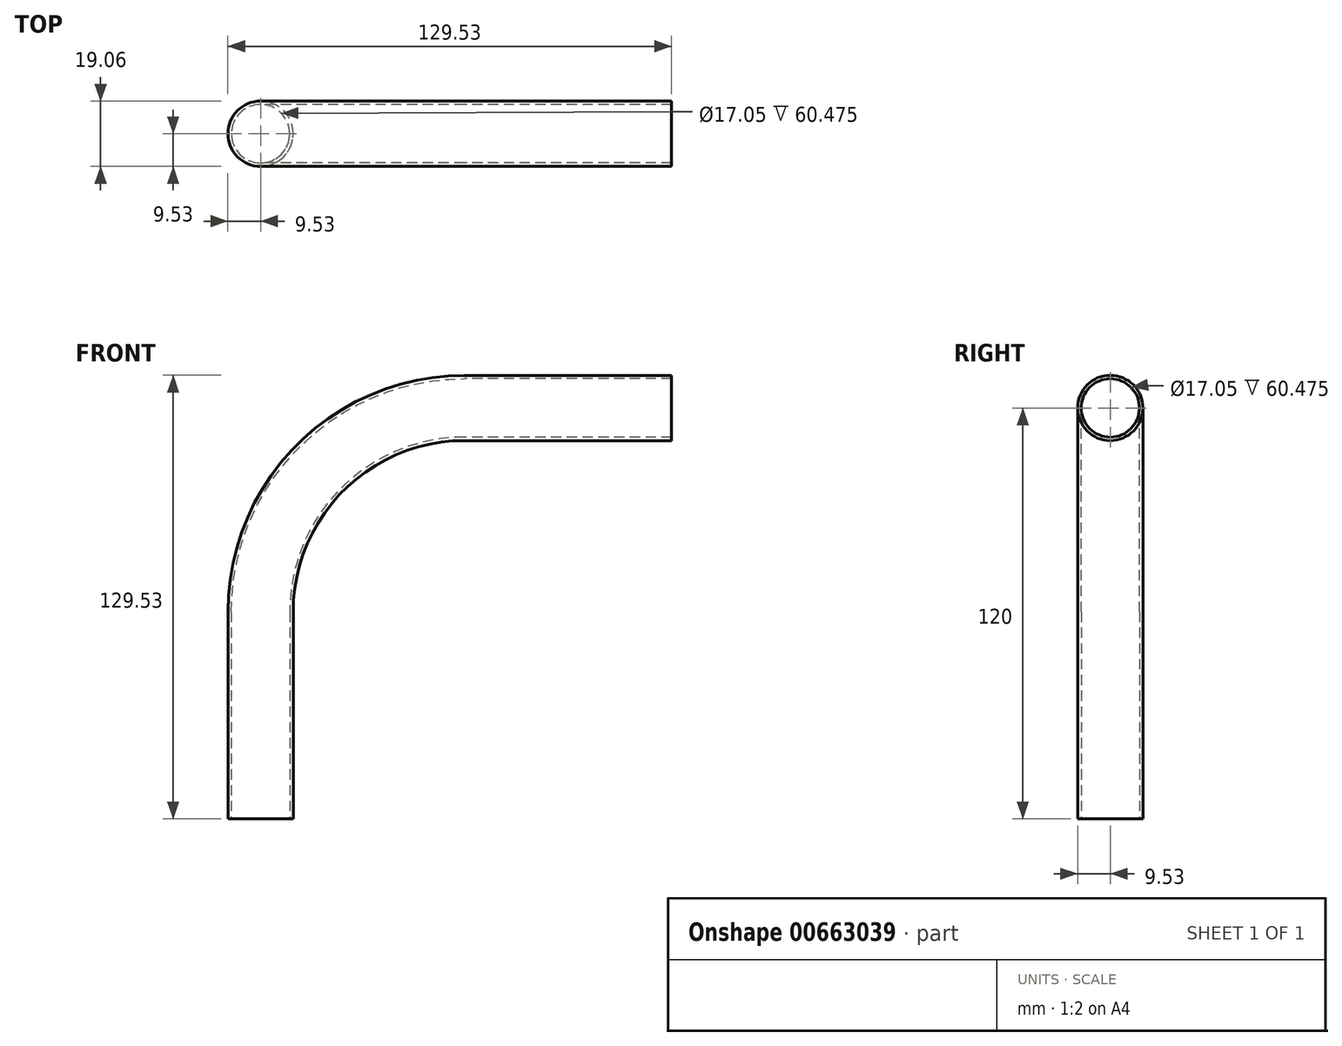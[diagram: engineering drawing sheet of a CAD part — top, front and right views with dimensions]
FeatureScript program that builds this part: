
annotation { "Feature Type Name" : "Feature", "Feature Type Description" : "" }
export const myFeature = defineFeature(function(context is Context, id is Id, definition is map)
    precondition{}
    {
        {
            var Q0;
            Q0=qCreatedBy(makeId("Front.planeOp"),FACE);
            var sketch = newSketch(context, id + "F0", { "sketchPlane" : qUnion([Q0])});
            skLineSegment(sketch, "E0", {"start": v(0, 0) * mm, "end": v(0, 60.47) * mm});
            skLineSegment(sketch, "E1", {"start": v(59.53, 120) * mm, "end": v(120, 120) * mm});
            skPoint(sketch, "E2.visualSharp", {"position": v(0, 120) * mm});
            skArc(sketch, "E2.filletArc", {"start": v(59.53, 120) * mm, "mid": v(17.43, 102.57) * mm, "end": v(0, 60.48) * mm});
            skSolve(sketch);
        }
        {
            var Q0;
            Q0=sQuery(id+"F0.wireOp",VERTEX,"E1.end");
            var Q1;
            Q1=qCreatedBy(makeId("Right.planeOp"),FACE);
            cPlane(context, id + "F1", {"entities" : qUnion([Q0, Q1]), "cplaneType" : CPlaneType.PLANE_POINT, "offset" : 25 * mm, "width" : 150 * mm, "height" : 150 * mm});
        }
        {
            var Q0;
            Q0=qCreatedBy(id+"F1.planeOp",FACE);
            var sketch = newSketch(context, id + "F2", { "sketchPlane" : qUnion([Q0])});
            skPoint(sketch, "E3", {"position": v(0, 120) * mm});
            skCircle(sketch, "E4", {"center": v(0, 120) * mm, "radius": 9.53 * mm});
            skCircle(sketch, "E5.0", {"center": v(0, 120) * mm, "radius": 8.53 * mm});
            skSolve(sketch);
        }
        {
            var Q0;
            Q0=makeQuery(id+"F2.imprint","IMPRINT",FACE,{"disambiguationData":[TD([[makeQuery(id+"F2.imprint","IMPRINT",EDGE,{"derivedFrom":sQuery(id+"F2.wireOp",EDGE,"E4")}),1.0]])]});
            var Q1;
            Q1=sQuery(id+"F0.wireOp",EDGE,"E1");
            var Q2;
            Q2=sQuery(id+"F0.wireOp",EDGE,"E2.filletArc");
            var Q3;
            Q3=sQuery(id+"F0.wireOp",EDGE,"E0");
            sweep(context, id + "F3", {"profiles" : qUnion([Q0]), "path" : qUnion([Q1, Q2, Q3])});
        }
    });
